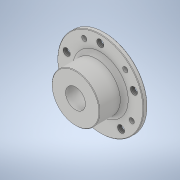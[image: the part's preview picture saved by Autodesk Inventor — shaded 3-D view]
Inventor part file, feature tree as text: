
AUTODESK INVENTOR PART (.ipt)
format: ipt  version: 2021 (Build 250183000, 183)  size: 217,088 bytes
history: native  units: in
note: dims shown in document units (in); Inventor stores cm internally (conversion verified against a paired STEP export)
features: thread x6, sketch x6, extrude x5, fillet x2, revolve x1, chamfer x1
ambient origin geometry x8: Origin, YZ Plane, XZ Plane, XY Plane, X Axis, Y Axis, Z Axis, Center Point
bodies: Solid1 (feature_tree)
feature tree (21):
  revolve  "Revolution1"  [1 undecoded]
  extrude  "Extrusion1"  Depth=0.26in
  extrude  "Extrusion2"  Depth=0.2in
  fillet  "Fillet1"  Radius=0.16in
  chamfer  "Chamfer1"  Distance=1.0in
  fillet  "Fillet2"  Radius=1.25in
  extrude  "Extrusion3"  Depth=0.25in TaperAngle=0.0deg
  thread  "Thread1"  [1 undecoded]
  thread  "Thread2"  [1 undecoded]
  thread  "Thread3"  [1 undecoded]
  thread  "Thread4"  [1 undecoded]
  thread  "Thread5"  [1 undecoded]
  thread  "Thread6"  [1 undecoded]
  extrude  "Extrusion4"  TaperAngle=45.0deg  [1 undecoded]
  extrude  "Extrusion5"  Depth=0.25in
  sketch  "Sketch1"  dims[d0=1.5in d1=1.56in]
  sketch  "Sketch2"  dims[d2=1.2in d3=0.26in]
  sketch  "Sketch3"  dims[d4=1.42in d5=0.2in d6=0.16in]
  sketch  "Sketch4"  dims[d7=0.52in]
  sketch  "Sketch5"  dims[d8=90.0deg]
  sketch  "Sketch6"  dims[d9=2.0in d10=1.0in d11=0.0in d12=1.25in d13=1.0in d14=0.0in d15=0.075in d16=0.03in d17=0.125in d18=45.0deg d19=0.25in d20=0.452in d21=0.48in d22=1.9685in d24=360.0deg d26=45.0deg d27=0.2in d28=0.2in d29=0.0in d30=0.435in d31=0.0in d32=0.435in d33=0.0in d34=0.435in d35=0.0in d36=0.435in d37=0.0in d38=0.435in d39=0.0in d40=0.435in d41=0.0in d42=1.0in d43=0.0in d44=0.325in d45=1.9685in d47=360.0deg d49=1.0in d50=0.0in]
note: 8 required parameter values undecoded (feature->parameter linkage not recoverable at this tier; creation-order binding heuristic only, values carry confidence <= 0.55)